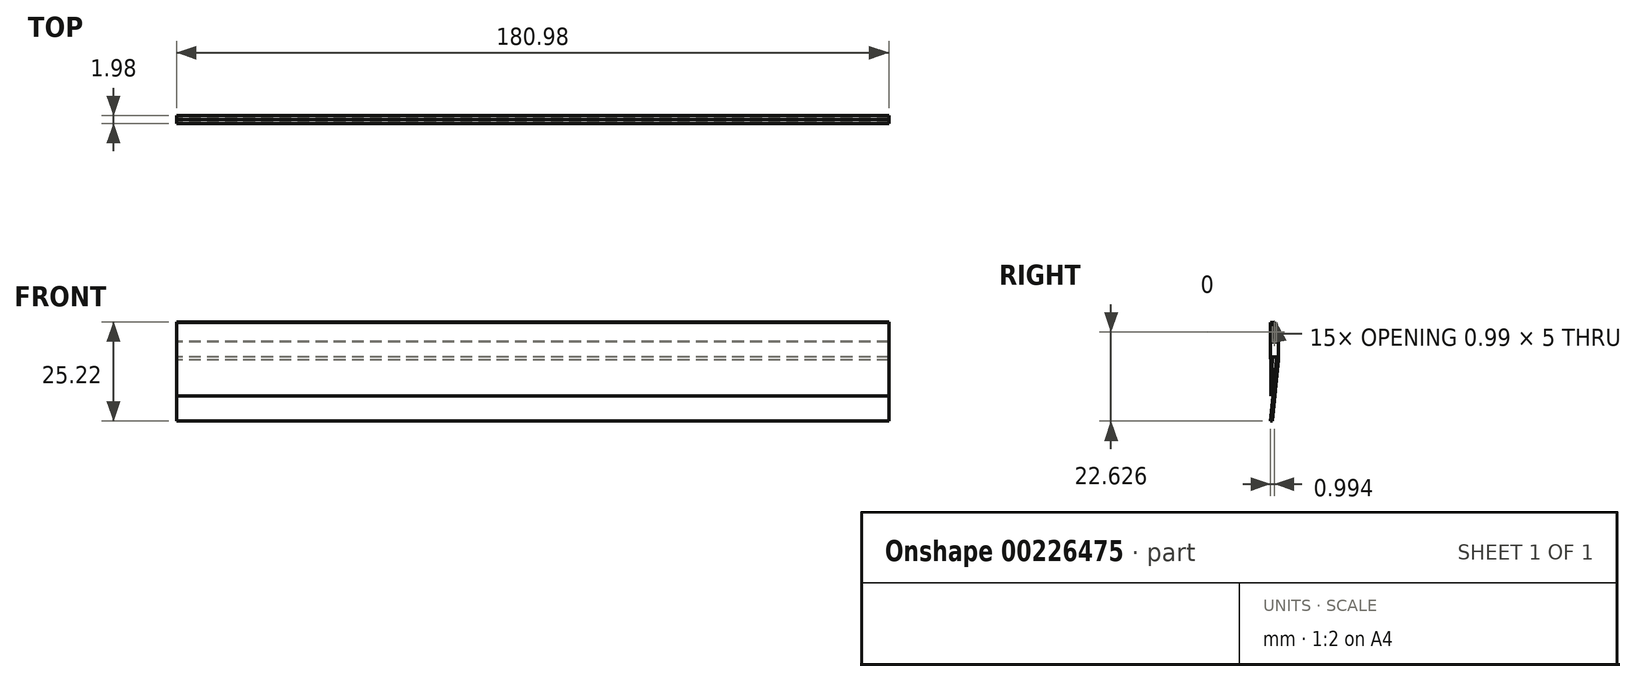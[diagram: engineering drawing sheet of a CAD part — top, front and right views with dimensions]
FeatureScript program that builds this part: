
annotation { "Feature Type Name" : "Feature", "Feature Type Description" : "" }
export const myFeature = defineFeature(function(context is Context, id is Id, definition is map)
    precondition{}
    {
        {
            var Q0;
            Q0=qCreatedBy(makeId("Right.planeOp"),FACE);
            var sketch = newSketch(context, id + "F0", { "sketchPlane" : qUnion([Q0])});
            skPoint(sketch, "E0.1", {"position": v(-11.89, -143.03) * mm});
            skPoint(sketch, "E0.2", {"position": v(-15.83, -142.6) * mm});
            skPoint(sketch, "E0.3", {"position": v(-10.97, -91.82) * mm});
            skPoint(sketch, "E0.4", {"position": v(-14.94, -92.03) * mm});
            skPoint(sketch, "E0.5", {"position": v(-3.94, -12.03) * mm});
            skPoint(sketch, "E0.6", {"position": v(-3.94, -18.53) * mm});
            skPoint(sketch, "E0.7", {"position": v(-11.84, -12.03) * mm});
            skPoint(sketch, "E0.8", {"position": v(0, -18.75) * mm});
            skPoint(sketch, "E0.9", {"position": v(0, 18.75) * mm});
            skPoint(sketch, "E0.10", {"position": v(-3.94, 18.35) * mm});
            skPoint(sketch, "E0.11", {"position": v(-11.84, 17.97) * mm});
            skPoint(sketch, "E1.0", {"position": v(-7.95, 58.75) * mm});
            skPoint(sketch, "E2.0", {"position": v(-11.84, 57.97) * mm});
            skPoint(sketch, "E3.0", {"position": v(-15.82, 57.97) * mm});
            skLineSegment(sketch, "E4", {"start": v(-11.89, -143.03) * mm, "end": v(0, -18.75) * mm});
            skLineSegment(sketch, "E5", {"start": v(0, 18.75) * mm, "end": v(-7.95, 58.75) * mm});
            skLineSegment(sketch, "E6", {"start": v(0, 18.75) * mm, "end": v(0, -18.75) * mm});
            skCircle(sketch, "E7", {"center": v(-11.84, 57.97) * mm, "radius": 3.96 * mm});
            skLineSegment(sketch, "E8", {"start": v(-15.82, 57.97) * mm, "end": v(-14.94, -92.03) * mm});
            skLineSegment(sketch, "E9", {"start": v(-11.84, -12.03) * mm, "end": v(-14.94, -92.03) * mm});
            skLineSegment(sketch, "E10", {"start": v(-3.94, -12.03) * mm, "end": v(-11.84, -12.03) * mm});
            skLineSegment(sketch, "E11", {"start": v(-3.94, -12.03) * mm, "end": v(-3.94, -18.53) * mm});
            skLineSegment(sketch, "E12", {"start": v(-3.94, -18.53) * mm, "end": v(-10.97, -91.82) * mm});
            skLineSegment(sketch, "E13", {"start": v(-10.97, -91.82) * mm, "end": v(-14.94, -92.03) * mm});
            skLineSegment(sketch, "E14", {"start": v(-15.83, -142.6) * mm, "end": v(-11.89, -143.03) * mm});
            skLineSegment(sketch, "E15", {"start": v(-15.83, -142.6) * mm, "end": v(-10.97, -91.82) * mm});
            skLineSegment(sketch, "E16", {"start": v(-3.94, 18.35) * mm, "end": v(-11.84, 57.97) * mm});
            skLineSegment(sketch, "E17", {"start": v(-11.84, 17.97) * mm, "end": v(-11.84, 57.97) * mm});
            skLineSegment(sketch, "E18", {"start": v(-3.94, 18.35) * mm, "end": v(-11.84, 17.97) * mm});
            skLineSegment(sketch, "E19", {"start": v(-7.95, 58.75) * mm, "end": v(-15.82, 57.97) * mm});
            skSolve(sketch);
        }
        {
            var Q0;
            Q0=makeQuery(id+"F0.imprint","IMPRINT",FACE,{"disambiguationData":[TD([[makeQuery(id+"F0.imprint","IMPRINT",EDGE,{"derivedFrom":sQuery(id+"F0.wireOp",EDGE,"E4")}),1.0]])]});
            var Q1;
            {var subQ0=sQuery(id+"F0.wireOp",EDGE,"E19");var subQ1=sQuery(id+"F0.wireOp",EDGE,"E7");var subQ2=makeQuery(id+"F0.imprint","INTERSECT",VERTEX,{"disambiguationData":[OD(0.0)],"derivedFrom":[subQ1,subQ0]});Q1=makeQuery(id+"F0.imprint","IMPRINT",FACE,{"disambiguationData":[TD([[makeQuery(id+"F0.imprint","IMPRINT",EDGE,{"disambiguationData":[TD([[subQ2,-1.0]])],"derivedFrom":subQ1}),1.0]])]});}
            var Q2;
            {var subQ0=sQuery(id+"F0.wireOp",EDGE,"E7");var subQ1=makeQuery(id+"F0.imprint","INTERSECT",VERTEX,{"derivedFrom":[sQuery(id+"F0.wireOp",EDGE,"E5"),subQ0]});Q2=makeQuery(id+"F0.imprint","IMPRINT",FACE,{"disambiguationData":[TD([[makeQuery(id+"F0.imprint","IMPRINT",EDGE,{"disambiguationData":[TD([[subQ1,-1.0]])],"derivedFrom":subQ0}),1.0]])]});}
            extrude(context, id + "F1", {"entities" : qUnion([Q0, Q1, Q2]), "depth" : 1447.8 * mm, "symmetric" : true});
        }
        {
            var Q0;
            Q0=makeQuery(id+"F1.opExtrude","SWEPT_BODY",BODY,{"disambiguationData":[OSD([sQuery(id+"F0.wireOp",EDGE,"E4"),sQuery(id+"F0.wireOp",EDGE,"E5"),sQuery(id+"F0.wireOp",EDGE,"E6"),sQuery(id+"F0.wireOp",EDGE,"E7"),sQuery(id+"F0.wireOp",EDGE,"E8"),sQuery(id+"F0.wireOp",EDGE,"E9"),sQuery(id+"F0.wireOp",EDGE,"E10"),sQuery(id+"F0.wireOp",EDGE,"E11"),sQuery(id+"F0.wireOp",EDGE,"E12"),sQuery(id+"F0.wireOp",EDGE,"E14"),sQuery(id+"F0.wireOp",EDGE,"E15"),sQuery(id+"F0.wireOp",EDGE,"E16"),sQuery(id+"F0.wireOp",EDGE,"E17"),sQuery(id+"F0.wireOp",EDGE,"E18"),sQuery(id+"F0.wireOp",EDGE,"E19")])]});
            var Q1;
            Q1=qCreatedBy(makeId("Origin.pointOp"),VERTEX);
            transform(context, id + "F2", {"entities" : qUnion([Q0]), "transformType" : TransformType.SCALE_UNIFORMLY, "scale" : 1 / 8, "scalePoint" : qUnion([Q1]), "makeCopy" : false});
        }
    });
